# Revit family: Layout-Teknion-Zones_Workstation_Integration_02-R2022
name_source: partatom
category: Furniture Systems
units: mm (PartAtom-declared; Revit-internal decimal feet)

## family parameters
Always vertical = Yes
Cut with Voids When Loaded = No
OmniClass Number = 23.40.70.14.64.21
OmniClass Title = Systems Furniture
Part Type = Normal
Room Calculation Point = No
Round Connector Dimension = Use Diameter
Shared = Yes
Work Plane-Based = No

## types (1)
- Layout-Teknion-Zones_Workstation_Integration_02-R2022
    Assembly Code = E2020200
    Brackets Height = 7.542 "
    Default Elevation = 0 "
    Description = 18'-0" x 12'-0"
    Manufacturer = Teknion
    Manufacturer Fax = 416.661.4586
    Model = Workstation Integration 02
    Product Line = Zones
    Product Page URL = http://teknionplanningtool.com
    Series = Zones
    Sustainability Data = http://www.teknion.com
    Table Top Height = 29 "
    URL = www.teknion.com
    Unit Weight URL = http://www.teknion.com
    Warranty = http://www.teknion.com
    Width = 68 "
    Worksurface Depth = 30 "
    Worksurface Width = 68 "

## geometry (parser evidence)
native form markers: Blend x136, Sweep x39
no freeform markers — native parametric forms only
